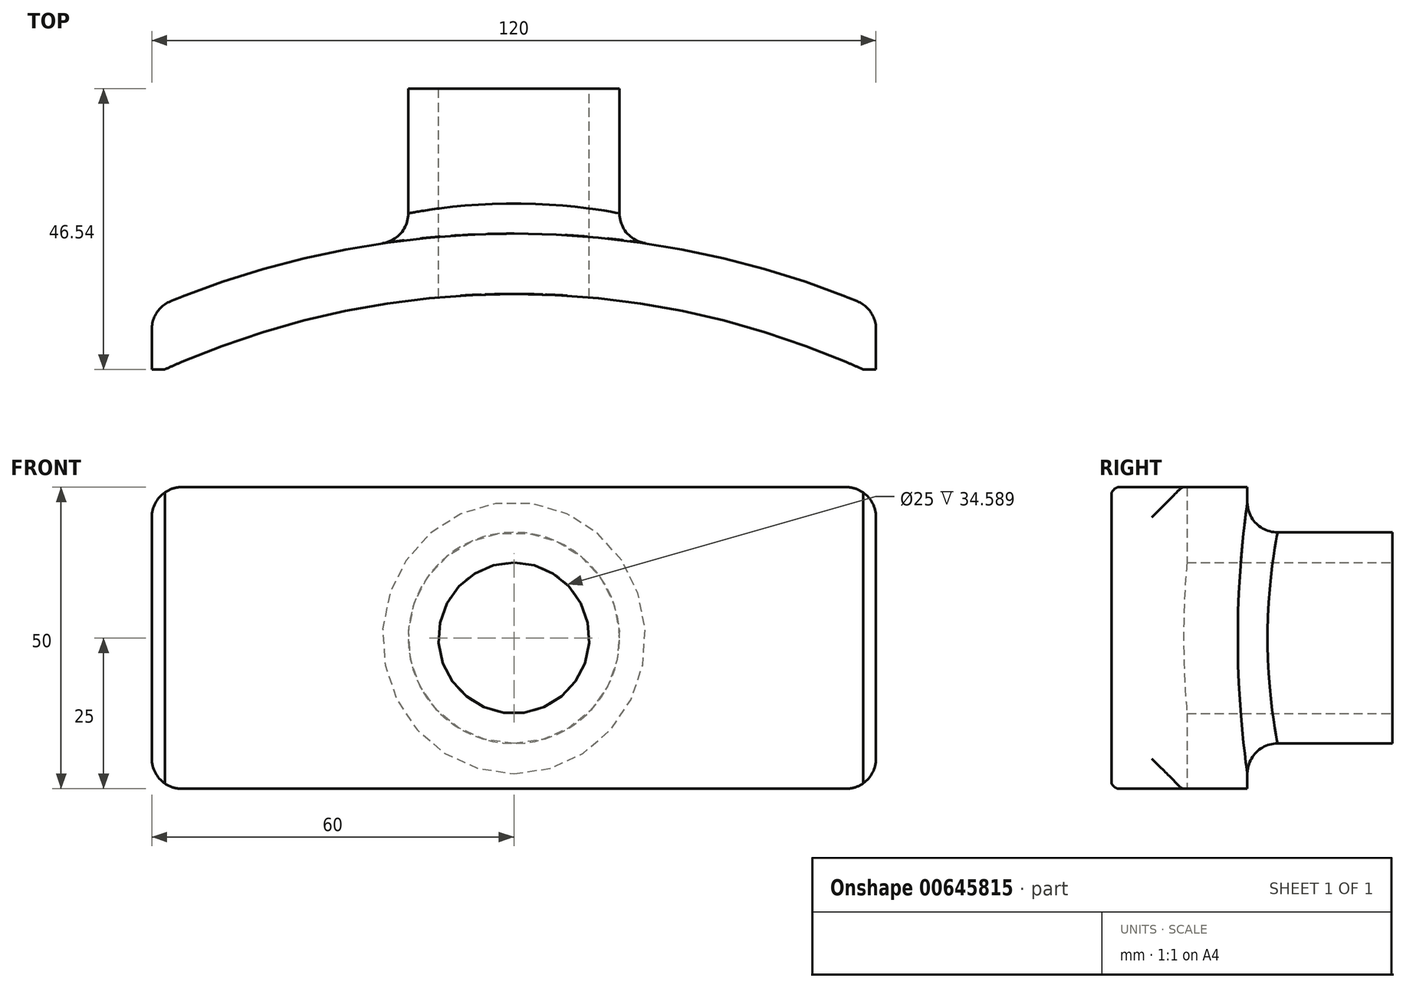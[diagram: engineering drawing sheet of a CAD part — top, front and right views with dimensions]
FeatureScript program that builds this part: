
annotation { "Feature Type Name" : "Feature", "Feature Type Description" : "" }
export const myFeature = defineFeature(function(context is Context, id is Id, definition is map)
    precondition{}
    {
        {
            var Q0;
            Q0=qCreatedBy(makeId("Top.planeOp"),FACE);
            var sketch = newSketch(context, id + "F0", { "sketchPlane" : qUnion([Q0])});
            skArc(sketch, "E0", {"start": v(57.84, 127.5) * mm, "mid": v(0, 140) * mm, "end": v(-57.84, 127.5) * mm});
            skArc(sketch, "E1", {"start": v(60, 137.48) * mm, "mid": v(0, 150) * mm, "end": v(-60, 137.48) * mm});
            skLineSegment(sketch, "E2", {"start": v(60, 126.5) * mm, "end": v(60, 137.48) * mm});
            skLineSegment(sketch, "E3", {"start": v(0, 0) * mm, "end": v(0, 112.63) * mm, "construction": true});
            skPoint(sketch, "E4.orphan", {"position": v(60, 0) * mm});
            skLineSegment(sketch, "E5.MirrorCS", {"start": v(-60, 127.5) * mm, "end": v(-60, 137.48) * mm});
            skPoint(sketch, "E6.orphan", {"position": v(-60, 126.5) * mm});
            skPoint(sketch, "E7.orphan", {"position": v(60, 126.5) * mm});
            skLineSegment(sketch, "E8", {"start": v(-67.9, 127.5) * mm, "end": v(-57.84, 127.5) * mm});
            skLineSegment(sketch, "E9.trimOffspring", {"start": v(57.84, 127.5) * mm, "end": v(60, 127.5) * mm});
            skSolve(sketch);
        }
        {
            var Q0;
            Q0=makeQuery(id+"F0.imprint","IMPRINT",FACE,{"disambiguationData":[TD([[makeQuery(id+"F0.imprint","IMPRINT",EDGE,{"derivedFrom":sQuery(id+"F0.wireOp",EDGE,"E0")}),-1.0]])]});
            extrude(context, id + "F1", {"entities" : qUnion([Q0]), "depth" : 50 * mm, "offsetDistance" : 25 * mm});
        }
        {
            var Q0;
            Q0=qCreatedBy(makeId("Front.planeOp"),FACE);
            var sketch = newSketch(context, id + "F2", { "sketchPlane" : qUnion([Q0])});
            skPoint(sketch, "E10", {"position": v(0, 25) * mm});
            skCircle(sketch, "E11", {"center": v(0, 25) * mm, "radius": 17.5 * mm});
            skSolve(sketch);
        }
        {
            var Q0;
            Q0=qSketchRegion(id+"F2",true);
            extrude(context, id + "F3", {"entities" : qUnion([Q0]), "operationType" : NewBodyOperationType.ADD, "oppositeDirection" : true, "depth" : 174.03 * mm, "offsetDistance" : 25 * mm, "hasSecondDirection" : true, "secondDirectionOppositeDirection" : true, "secondDirectionDepth" : 144.73 * mm});
        }
        {
            var Q0;
            Q0=makeQuery(id+"F3.boolean.opBoolean","INTERSECT",EDGE,{"derivedFrom":[makeQuery(id+"F1.opExtrude","SWEPT_FACE",FACE,{"disambiguationData":[OSD([sQuery(id+"F0.wireOp",EDGE,"E1")])]}),makeQuery(id+"F3.opExtrude","SWEPT_FACE",FACE,{"disambiguationData":[OSD([sQuery(id+"F2.wireOp",EDGE,"E11")])]})]});
            fillet(context, id + "F4", {"entities" : qUnion([Q0]), "radius" : 5 * mm, "tangentPropagation" : true, "allowEdgeOverflow" : false});
        }
        {
            var Q0;
            Q0=makeQuery(id+"F3.opExtrude","CAP_FACE",FACE,{"disambiguationData":[OSD([sQuery(id+"F2.wireOp",EDGE,"E11")])],"isStart":false});
            var sketch = newSketch(context, id + "F5", { "sketchPlane" : qUnion([Q0])});
            skPoint(sketch, "E12", {"position": v(0, 25) * mm});
            skSolve(sketch);
        }
        {
            var Q0;
            Q0=sQuery(id+"F5.wireOp",VERTEX,"E12");
            var Q1;
            Q1=makeQuery(id+"F1.opExtrude","SWEPT_BODY",BODY,{"disambiguationData":[OSD([sQuery(id+"F0.wireOp",EDGE,"E0"),sQuery(id+"F0.wireOp",EDGE,"E1"),sQuery(id+"F0.wireOp",EDGE,"E2"),sQuery(id+"F0.wireOp",EDGE,"E5.MirrorCS")])]});
            hole(context, id + "F6", {"style" : HoleStyle.SIMPLE, "endStyle" : HoleEndStyle.THROUGH, "holeDiameter" : 25 * mm, "majorDiameter" : 5 * mm, "isTappedThrough" : true, "tappedDepth" : 12 * mm, "tapClearance" : 3, "locations" : qUnion([Q0]), "scope" : qUnion([Q1])});
        }
        {
            var Q0;
            Q0=makeQuery(id+"F1.opExtrude","CAP_EDGE",EDGE,{"disambiguationData":[OSD([sQuery(id+"F0.wireOp",EDGE,"E5.MirrorCS")])],"isStart":false});
            var Q1;
            Q1=makeQuery(id+"F1.opExtrude","SWEPT_EDGE",EDGE,{"disambiguationData":[OSD([sQuery(id+"F0.wireOp",EDGE,"E1"),sQuery(id+"F0.wireOp",EDGE,"E5.MirrorCS")])]});
            var Q2;
            Q2=makeQuery(id+"F1.opExtrude","CAP_EDGE",EDGE,{"disambiguationData":[OSD([sQuery(id+"F0.wireOp",EDGE,"E5.MirrorCS")])],"isStart":true});
            var Q3;
            Q3=makeQuery(id+"F1.opExtrude","CAP_EDGE",EDGE,{"disambiguationData":[OSD([sQuery(id+"F0.wireOp",EDGE,"E2")])],"isStart":false});
            var Q4;
            Q4=makeQuery(id+"F1.opExtrude","SWEPT_EDGE",EDGE,{"disambiguationData":[OSD([sQuery(id+"F0.wireOp",EDGE,"E1"),sQuery(id+"F0.wireOp",EDGE,"E2")])]});
            var Q5;
            Q5=makeQuery(id+"F1.opExtrude","CAP_EDGE",EDGE,{"disambiguationData":[OSD([sQuery(id+"F0.wireOp",EDGE,"E2")])],"isStart":true});
            fillet(context, id + "F7", {"entities" : qUnion([Q0, Q1, Q2, Q3, Q4, Q5]), "radius" : 5 * mm, "tangentPropagation" : true, "allowEdgeOverflow" : false});
        }
    });
